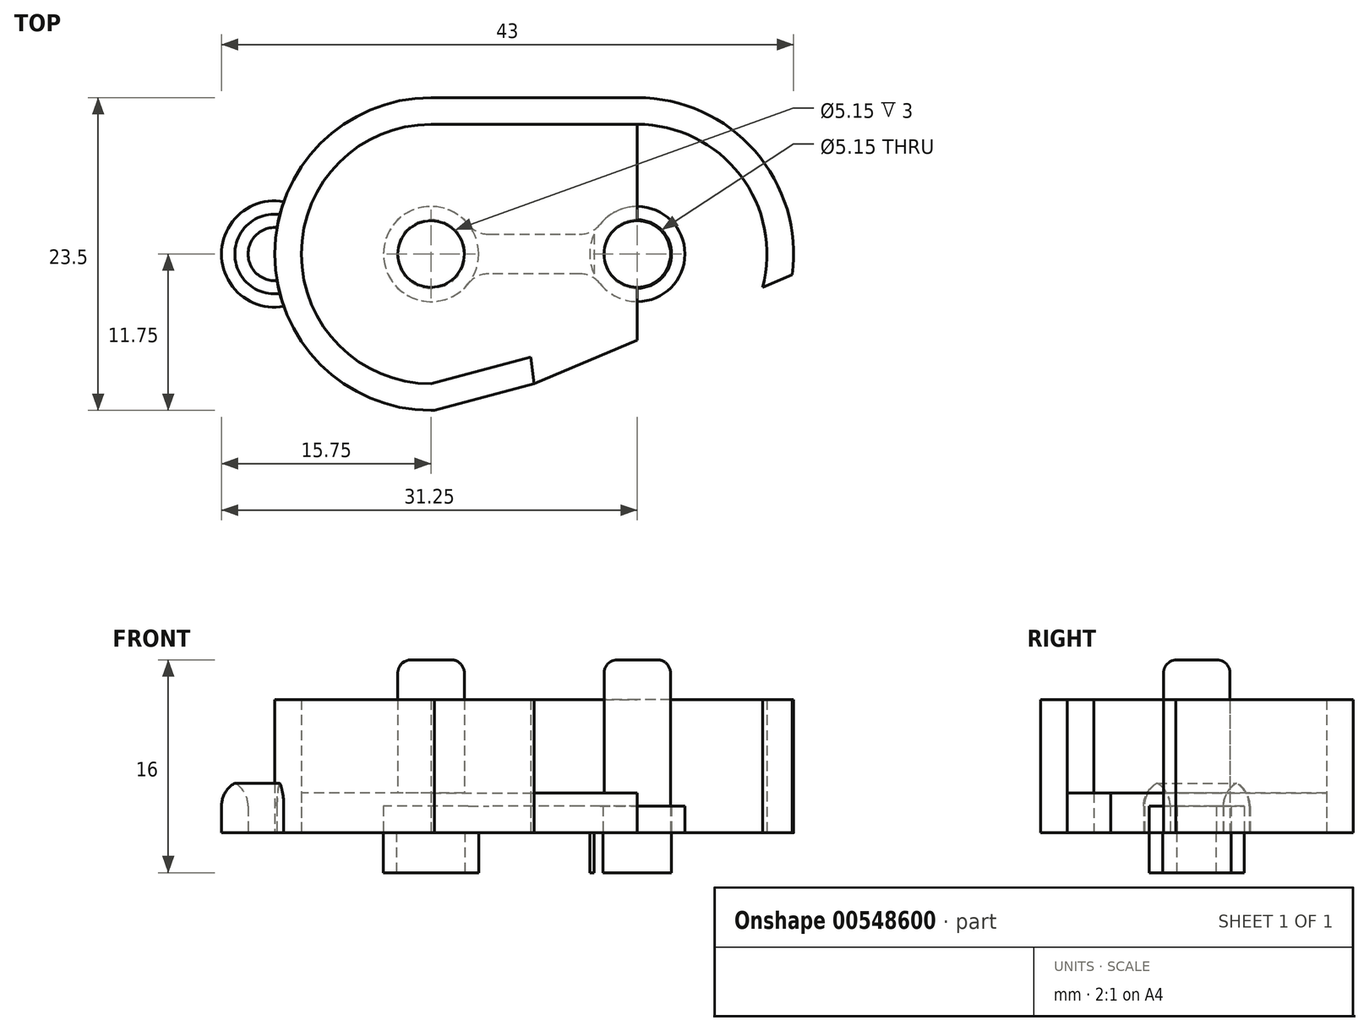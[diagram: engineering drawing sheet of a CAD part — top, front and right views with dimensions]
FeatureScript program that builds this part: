
annotation { "Feature Type Name" : "Feature", "Feature Type Description" : "" }
export const myFeature = defineFeature(function(context is Context, id is Id, definition is map)
    precondition{}
    {
        {
            var Q0;
            Q0=qCreatedBy(makeId("Top.planeOp"),FACE);
            var sketch = newSketch(context, id + "F0", { "sketchPlane" : qUnion([Q0])});
            skArc(sketch, "E0", {"start": v(-7.75, 11.75) * mm, "mid": v(-19.5, 0) * mm, "end": v(-7.75, -11.75) * mm});
            skPoint(sketch, "E1", {"position": v(-19.5, 0) * mm});
            skPoint(sketch, "E2.MirrorP", {"position": v(19.5, 0) * mm});
            skLineSegment(sketch, "E3", {"start": v(-7.75, 11.75) * mm, "end": v(-7.75, 0) * mm});
            skLineSegment(sketch, "E4", {"start": v(-7.75, -11.75) * mm, "end": v(-7.75, 0) * mm});
            skCircle(sketch, "E5", {"center": v(-7.75, 0) * mm, "radius": 2.5 * mm});
            skArc(sketch, "E6", {"start": v(-7.75, 9.75) * mm, "mid": v(-17.5, 0) * mm, "end": v(-7.75, -9.75) * mm});
            skLineSegment(sketch, "E7", {"start": v(-7.75, 9.75) * mm, "end": v(0, 9.75) * mm});
            skLineSegment(sketch, "E8", {"start": v(-7.75, 11.75) * mm, "end": v(0, 11.75) * mm});
            skLineSegment(sketch, "E9", {"start": v(-7.75, -9.75) * mm, "end": v(0, -9.75) * mm});
            skLineSegment(sketch, "E10", {"start": v(-7.75, -11.75) * mm, "end": v(0, -11.75) * mm});
            skArc(sketch, "E11.MirrorCS", {"start": v(7.75, 11.75) * mm, "mid": v(19.5, 0) * mm, "end": v(7.75, -11.75) * mm});
            skLineSegment(sketch, "E12.MirrorCS", {"start": v(7.75, 11.75) * mm, "end": v(7.75, 0) * mm});
            skLineSegment(sketch, "E13.MirrorCS", {"start": v(7.75, 11.75) * mm, "end": v(0, 11.75) * mm});
            skLineSegment(sketch, "E14.MirrorCS", {"start": v(7.75, -9.75) * mm, "end": v(0, -9.75) * mm});
            skArc(sketch, "E15.MirrorCS", {"start": v(7.75, 9.75) * mm, "mid": v(17.5, 0) * mm, "end": v(7.75, -9.75) * mm});
            skCircle(sketch, "E16.MirrorC", {"center": v(7.75, 0) * mm, "radius": 2.5 * mm});
            skLineSegment(sketch, "E17.MirrorCS", {"start": v(7.75, -11.75) * mm, "end": v(7.75, 0) * mm});
            skLineSegment(sketch, "E18.MirrorCS", {"start": v(7.75, -11.75) * mm, "end": v(0, -11.75) * mm});
            skLineSegment(sketch, "E19.MirrorCS", {"start": v(7.75, 9.75) * mm, "end": v(0, 9.75) * mm});
            skLineSegment(sketch, "E20", {"start": v(-7.49, -11.75) * mm, "end": v(0, -9.75) * mm});
            skLineSegment(sketch, "E21", {"start": v(-7.75, -9.75) * mm, "end": v(-0.26, -7.75) * mm});
            skLineSegment(sketch, "E22", {"start": v(-0.26, -7.75) * mm, "end": v(0, -9.75) * mm});
            skLineSegment(sketch, "E23", {"start": v(19.4, -1.57) * mm, "end": v(0, -9.75) * mm});
            skLineSegment(sketch, "E24", {"start": v(-7.49, -11.75) * mm, "end": v(19.5, -11.75) * mm});
            skLineSegment(sketch, "E25", {"start": v(19.5, -11.75) * mm, "end": v(19.4, -1.57) * mm});
            skLineSegment(sketch, "E26", {"start": v(17.5, 0) * mm, "end": v(19.4, -1.57) * mm});
            skArc(sketch, "E27", {"start": v(-19.33, 2) * mm, "mid": v(-21.5, 0) * mm, "end": v(-19.33, -2) * mm});
            skArc(sketch, "E28", {"start": v(-18.82, 3.94) * mm, "mid": v(-23.5, 0) * mm, "end": v(-18.82, -3.94) * mm});
            skSolve(sketch);
        }
        {
            var Q0;
            {var subQ0=sQuery(id+"F0.wireOp",EDGE,"E0");Q0=makeQuery(id+"F0.imprint","IMPRINT",FACE,{"disambiguationData":[TD([[makeQuery(id+"F0.imprint","IMPRINT",EDGE,{"derivedFrom":subQ0}),1.0]])]});}
            var Q1;
            {var subQ0=sQuery(id+"F0.wireOp",EDGE,"E7");Q1=makeQuery(id+"F0.imprint","IMPRINT",FACE,{"disambiguationData":[TD([[makeQuery(id+"F0.imprint","IMPRINT",EDGE,{"derivedFrom":subQ0}),1.0]])]});}
            var Q2;
            {var subQ2=sQuery(id+"F0.wireOp",EDGE,"E9");Q2=makeQuery(id+"F0.imprint","IMPRINT",FACE,{"disambiguationData":[TD([[makeQuery(id+"F0.imprint","IMPRINT",EDGE,{"derivedFrom":subQ2}),-1.0]])]});}
            var Q3;
            Q3=makeQuery(id+"F0.imprint","IMPRINT",FACE,{"disambiguationData":[TD([[makeQuery(id+"F0.imprint","IMPRINT",EDGE,{"derivedFrom":sQuery(id+"F0.wireOp",EDGE,"E9")}),1.0]])]});
            var Q4;
            {var subQ3=sQuery(id+"F0.wireOp",EDGE,"E26");Q4=makeQuery(id+"F0.imprint","IMPRINT",FACE,{"disambiguationData":[TD([[makeQuery(id+"F0.imprint","IMPRINT",EDGE,{"derivedFrom":subQ3}),1.0]])]});}
            var Q5;
            {var subQ0=sQuery(id+"F0.wireOp",EDGE,"E26");Q5=makeQuery(id+"F0.imprint","IMPRINT",FACE,{"disambiguationData":[TD([[makeQuery(id+"F0.imprint","IMPRINT",EDGE,{"derivedFrom":subQ0}),-1.0]])]});}
            extrude(context, id + "F1", {"entities" : qUnion([Q0, Q1, Q2, Q3, Q4, Q5]), "depth" : 10 * mm, "offsetDistance" : 25 * mm});
        }
        {
            var Q0;
            {var subQ0=sQuery(id+"F0.wireOp",EDGE,"E6");Q0=makeQuery(id+"F0.imprint","IMPRINT",FACE,{"disambiguationData":[TD([[makeQuery(id+"F0.imprint","IMPRINT",EDGE,{"derivedFrom":subQ0}),1.0]])]});}
            var Q1;
            {var subQ6=sQuery(id+"F0.wireOp",EDGE,"E7");Q1=makeQuery(id+"F0.imprint","IMPRINT",FACE,{"disambiguationData":[TD([[makeQuery(id+"F0.imprint","IMPRINT",EDGE,{"derivedFrom":subQ6}),-1.0]])]});}
            var Q2;
            {var subQ0=sQuery(id+"F0.wireOp",EDGE,"E16.MirrorC");var subQ1=sQuery(id+"F0.wireOp",EDGE,"E12.MirrorCS");var subQ2=makeQuery(id+"F0.imprint","INTERSECT",VERTEX,{"derivedFrom":[subQ1,subQ0]});Q2=makeQuery(id+"F0.imprint","IMPRINT",FACE,{"disambiguationData":[TD([[makeQuery(id+"F0.imprint","IMPRINT",EDGE,{"disambiguationData":[TD([[subQ2,-1.0]])],"derivedFrom":subQ0}),1.0]])]});}
            extrude(context, id + "F2", {"entities" : qUnion([Q0, Q1, Q2]), "depth" : 3 * mm, "offsetDistance" : 25 * mm});
        }
        {
            var Q0;
            {var subQ0=sQuery(id+"F0.wireOp",EDGE,"E27");Q0=makeQuery(id+"F0.imprint","IMPRINT",FACE,{"disambiguationData":[TD([[makeQuery(id+"F0.imprint","IMPRINT",EDGE,{"derivedFrom":subQ0}),-1.0]])]});}
            extrude(context, id + "F3", {"entities" : qUnion([Q0]), "operationType" : NewBodyOperationType.ADD, "depth" : 4 * mm, "offsetDistance" : 25 * mm});
        }
        {
            var Q0;
            Q0=makeQuery(id+"F3.opExtrude","CAP_EDGE",EDGE,{"disambiguationData":[OSD([sQuery(id+"F0.wireOp",EDGE,"E27")])],"isStart":false});
            var Q1;
            Q1=makeQuery(id+"F3.opExtrude","CAP_EDGE",EDGE,{"disambiguationData":[OSD([sQuery(id+"F0.wireOp",EDGE,"E28")])],"isStart":false});
            fillet(context, id + "F4", {"entities" : qUnion([Q0, Q1]), "radius" : 2 * mm, "tangentPropagation" : true, "allowEdgeOverflow" : false});
        }
        {
            var Q0;
            {var subQ0=sQuery(id+"F0.wireOp",EDGE,"E4");var subQ1=sQuery(id+"F0.wireOp",EDGE,"E3");var subQ2=makeQuery(id+"F0.imprint","INTERSECT",VERTEX,{"derivedFrom":[subQ1,subQ0]});Q0=makeQuery(id+"F0.imprint","IMPRINT",FACE,{"disambiguationData":[TD([[makeQuery(id+"F0.imprint","IMPRINT",EDGE,{"disambiguationData":[TD([[subQ2,1.0]])],"derivedFrom":subQ1}),1.0]])]});}
            var Q1;
            {var subQ0=sQuery(id+"F0.wireOp",EDGE,"E4");var subQ1=sQuery(id+"F0.wireOp",EDGE,"E3");var subQ2=makeQuery(id+"F0.imprint","INTERSECT",VERTEX,{"derivedFrom":[subQ1,subQ0]});Q1=makeQuery(id+"F0.imprint","IMPRINT",FACE,{"disambiguationData":[TD([[makeQuery(id+"F0.imprint","IMPRINT",EDGE,{"disambiguationData":[TD([[subQ2,1.0]])],"derivedFrom":subQ1}),-1.0]])]});}
            var Q2;
            {var subQ0=sQuery(id+"F0.wireOp",EDGE,"E17.MirrorCS");var subQ1=sQuery(id+"F0.wireOp",EDGE,"E12.MirrorCS");var subQ2=makeQuery(id+"F0.imprint","INTERSECT",VERTEX,{"derivedFrom":[subQ1,subQ0]});Q2=makeQuery(id+"F0.imprint","IMPRINT",FACE,{"disambiguationData":[TD([[makeQuery(id+"F0.imprint","IMPRINT",EDGE,{"disambiguationData":[TD([[subQ2,1.0]])],"derivedFrom":subQ1}),-1.0]])]});}
            var Q3;
            {var subQ0=sQuery(id+"F0.wireOp",EDGE,"E17.MirrorCS");var subQ1=sQuery(id+"F0.wireOp",EDGE,"E12.MirrorCS");var subQ2=makeQuery(id+"F0.imprint","INTERSECT",VERTEX,{"derivedFrom":[subQ1,subQ0]});Q3=makeQuery(id+"F0.imprint","IMPRINT",FACE,{"disambiguationData":[TD([[makeQuery(id+"F0.imprint","IMPRINT",EDGE,{"disambiguationData":[TD([[subQ2,1.0]])],"derivedFrom":subQ1}),1.0]])]});}
            extrude(context, id + "F5", {"entities" : qUnion([Q0, Q1, Q2, Q3]), "operationType" : NewBodyOperationType.ADD, "depth" : 13 * mm, "offsetDistance" : 25 * mm});
        }
        {
            var Q0;
            Q0=makeQuery(id+"F5.opExtrude","CAP_EDGE",EDGE,{"disambiguationData":[OSD([sQuery(id+"F0.wireOp",EDGE,"E5")])],"isStart":false});
            var Q1;
            Q1=makeQuery(id+"F5.opExtrude","CAP_EDGE",EDGE,{"disambiguationData":[OSD([sQuery(id+"F0.wireOp",EDGE,"E16.MirrorC")])],"isStart":false});
            fillet(context, id + "F6", {"entities" : qUnion([Q0, Q1]), "radius" : 1 * mm, "tangentPropagation" : true, "allowEdgeOverflow" : false});
        }
        {
            var Q0;
            Q0=qCreatedBy(makeId("Top.planeOp"),FACE);
            var sketch = newSketch(context, id + "F7", { "sketchPlane" : qUnion([Q0])});
            skCircle(sketch, "E29", {"center": v(-7.75, 0) * mm, "radius": 2.58 * mm});
            skCircle(sketch, "E30", {"center": v(-7.75, 0) * mm, "radius": 3.58 * mm});
            skCircle(sketch, "E31.MirrorC", {"center": v(7.75, 0) * mm, "radius": 3.58 * mm});
            skCircle(sketch, "E32.MirrorC", {"center": v(7.75, 0) * mm, "radius": 2.58 * mm});
            skLineSegment(sketch, "E33", {"start": v(-7.75, 0) * mm, "end": v(-7.75, 3.58) * mm});
            skLineSegment(sketch, "E34", {"start": v(-4.5, 1.48) * mm, "end": v(4.5, 1.48) * mm});
            skLineSegment(sketch, "E35", {"start": v(4.5, 1.48) * mm, "end": v(4.5, -1.48) * mm});
            skLineSegment(sketch, "E36", {"start": v(4.5, -1.48) * mm, "end": v(-4.5, -1.48) * mm});
            skSolve(sketch);
        }
        {
            var Q0;
            Q0 = qSketchRegion(id + "F7", true);
            var Q1;
            Q1=makeQuery(id+"F7.imprint","IMPRINT",FACE,{"disambiguationData":[TD([[makeQuery(id+"F7.imprint","IMPRINT",EDGE,{"derivedFrom":sQuery(id+"F7.wireOp",EDGE,"E29")}),1.0]])]});
            var Q2;
            Q2=makeQuery(id+"F7.imprint","IMPRINT",FACE,{"disambiguationData":[TD([[makeQuery(id+"F7.imprint","IMPRINT",EDGE,{"derivedFrom":sQuery(id+"F7.wireOp",EDGE,"E32.MirrorC")}),-1.0]])]});
            extrude(context, id + "F8", {"entities" : qUnion([Q0, Q1, Q2]), "depth" : 2 * mm, "offsetDistance" : 25 * mm});
        }
        {
            var Q0;
            Q0=makeQuery(id+"F7.imprint","IMPRINT",FACE,{"disambiguationData":[TD([[makeQuery(id+"F7.imprint","IMPRINT",EDGE,{"derivedFrom":sQuery(id+"F7.wireOp",EDGE,"E29")}),-1.0]])]});
            var Q1;
            Q1=makeQuery(id+"F7.imprint","IMPRINT",FACE,{"disambiguationData":[TD([[makeQuery(id+"F7.imprint","IMPRINT",EDGE,{"derivedFrom":sQuery(id+"F7.wireOp",EDGE,"E32.MirrorC")}),1.0]])]});
            var Q2;
            {var subQ0=sQuery(id+"F7.wireOp",EDGE,"E35");Q2=makeQuery(id+"F7.imprint","IMPRINT",FACE,{"disambiguationData":[TD([[makeQuery(id+"F7.imprint","IMPRINT",EDGE,{"derivedFrom":subQ0}),-1.0]])]});}
            extrude(context, id + "F9", {"entities" : qUnion([Q0, Q1, Q2]), "oppositeDirection" : true, "depth" : 3 * mm, "offsetDistance" : 25 * mm});
        }
        {
            var Q0;
            Q0=makeQuery(id+"F8.opExtrude","SWEPT_EDGE",EDGE,{"disambiguationData":[OSD([sQuery(id+"F7.wireOp",EDGE,"E30"),sQuery(id+"F7.wireOp",EDGE,"E34")])]});
            var Q1;
            Q1=makeQuery(id+"F8.opExtrude","SWEPT_EDGE",EDGE,{"disambiguationData":[OSD([sQuery(id+"F7.wireOp",EDGE,"E30"),sQuery(id+"F7.wireOp",EDGE,"E36")])]});
            var Q2;
            Q2=makeQuery(id+"F8.opExtrude","SWEPT_EDGE",EDGE,{"disambiguationData":[OSD([sQuery(id+"F7.wireOp",EDGE,"E31.MirrorC"),sQuery(id+"F7.wireOp",EDGE,"E35"),sQuery(id+"F7.wireOp",EDGE,"E36")])]});
            var Q3;
            Q3=makeQuery(id+"F8.opExtrude","SWEPT_EDGE",EDGE,{"disambiguationData":[OSD([sQuery(id+"F7.wireOp",EDGE,"E31.MirrorC"),sQuery(id+"F7.wireOp",EDGE,"E34"),sQuery(id+"F7.wireOp",EDGE,"E35")])]});
            fillet(context, id + "F10", {"entities" : qUnion([Q0, Q1, Q2, Q3]), "radius" : 2 * mm, "tangentPropagation" : true, "allowEdgeOverflow" : false});
        }
    });
